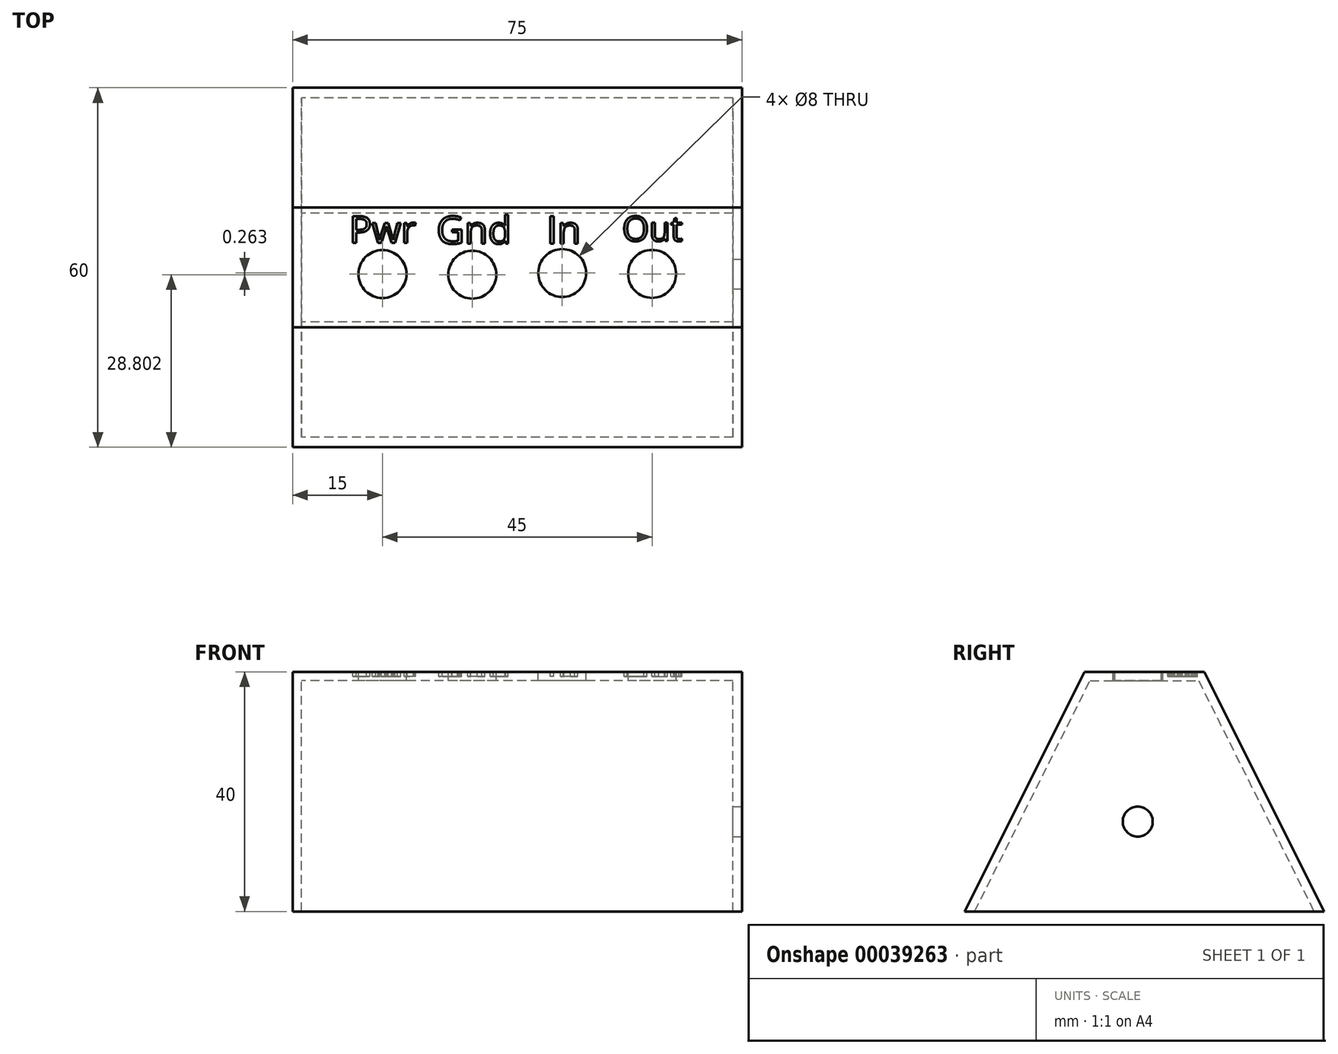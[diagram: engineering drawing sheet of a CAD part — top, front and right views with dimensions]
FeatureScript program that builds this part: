
annotation { "Feature Type Name" : "Feature", "Feature Type Description" : "" }
export const myFeature = defineFeature(function(context is Context, id is Id, definition is map)
    precondition{}
    {
        {
            var Q0;
            Q0=qCreatedBy(makeId("Right.planeOp"),FACE);
            var sketch = newSketch(context, id + "F0", { "sketchPlane" : qUnion([Q0])});
            skLineSegment(sketch, "E0", {"start": v(-28.9, 0) * mm, "end": v(-8.9, 40) * mm});
            skLineSegment(sketch, "E1", {"start": v(-8.9, 40) * mm, "end": v(11.1, 40) * mm});
            skLineSegment(sketch, "E2", {"start": v(11.1, 40) * mm, "end": v(31.1, 0) * mm});
            skLineSegment(sketch, "E3", {"start": v(31.1, 0) * mm, "end": v(-28.9, 0) * mm});
            skSolve(sketch);
        }
        {
            var Q0;
            Q0=makeQuery(id+"F0.imprint","IMPRINT",FACE,{"disambiguationData":[TD([[makeQuery(id+"F0.imprint","IMPRINT",EDGE,{"derivedFrom":sQuery(id+"F0.wireOp",EDGE,"E0")}),-1.0]])]});
            extrude(context, id + "F1", {"entities" : qUnion([Q0]), "depth" : 75 * mm});
        }
        {
            var Q0;
            Q0=makeQuery(id+"F1.opExtrude","SWEPT_FACE",FACE,{"disambiguationData":[OSD([sQuery(id+"F0.wireOp",EDGE,"E3")])]});
            shell(context, id + "F2", {"entities" : qUnion([Q0]), "thickness" : 1.5 * mm});
        }
        {
            var Q0;
            Q0=makeQuery(id+"F1.opExtrude","SWEPT_FACE",FACE,{"disambiguationData":[OSD([sQuery(id+"F0.wireOp",EDGE,"E1")])]});
            var sketch = newSketch(context, id + "F3", { "sketchPlane" : qUnion([Q0])});
            skPoint(sketch, "E4", {"position": v(15, 0) * mm});
            skPoint(sketch, "E5", {"position": v(30, -0.1) * mm});
            skPoint(sketch, "E6", {"position": v(45, 0.17) * mm});
            skPoint(sketch, "E7", {"position": v(60, 0.03) * mm});
            skSolve(sketch);
        }
        {
            var Q0;
            Q0=makeQuery(id+"F1.opExtrude","CAP_FACE",FACE,{"disambiguationData":[OSD([sQuery(id+"F0.wireOp",EDGE,"E0"),sQuery(id+"F0.wireOp",EDGE,"E1"),sQuery(id+"F0.wireOp",EDGE,"E2"),sQuery(id+"F0.wireOp",EDGE,"E3")])],"isStart":false});
            var sketch = newSketch(context, id + "F4", { "sketchPlane" : qUnion([Q0])});
            skPoint(sketch, "E8", {"position": v(0, 15) * mm});
            skSolve(sketch);
        }
        {
            var Q0;
            Q0=sQuery(id+"F4.wireOp",VERTEX,"E8");
            var Q1;
            Q1=makeQuery(id+"F1.opExtrude","SWEPT_BODY",BODY,{"disambiguationData":[OSD([sQuery(id+"F0.wireOp",EDGE,"E0"),sQuery(id+"F0.wireOp",EDGE,"E1"),sQuery(id+"F0.wireOp",EDGE,"E2"),sQuery(id+"F0.wireOp",EDGE,"E3")])]});
            hole(context, id + "F5", {"style" : HoleStyle.SIMPLE, "holeDiameter" : 5 * mm, "endStyle" : HoleEndStyle.BLIND, "holeDepth" : 20 * mm, "locations" : qUnion([Q0]), "scope" : qUnion([Q1])});
        }
        {
            var Q0;
            Q0=makeQuery(id+"F1.opExtrude","SWEPT_FACE",FACE,{"disambiguationData":[OSD([sQuery(id+"F0.wireOp",EDGE,"E1")])]});
            var sketch = newSketch(context, id + "F6", { "sketchPlane" : qUnion([Q0])});
            skText(sketch, "E9", { "text": "Out", "fontName": "OpenSans-Regular.ttf"});
            skText(sketch, "E10", { "text": "In", "fontName": "OpenSans-Regular.ttf"});
            skText(sketch, "E11", { "text": "Gnd", "fontName": "OpenSans-Regular.ttf"});
            skText(sketch, "E12", { "text": "Pwr", "fontName": "OpenSans-Regular.ttf"});
            const initialGuessF6  = {"E9": [0.055, 0.0055, 1, 0, 0.00417], "E10": [0.0424, 0.00506, 1, 0, 0.00462], "E11": [0.024, 0.00506, 1, 0, 0.00462], "E12": [0.00947, 0.00519, 1, 0, 0.0045]};
            skSetInitialGuess(sketch, initialGuessF6);
            skSolve(sketch);
        }
        {
            var Q0;
            Q0 = qSketchRegion(id + "F6", true);
            extrude(context, id + "F7", {"entities" : qUnion([Q0]), "operationType" : NewBodyOperationType.REMOVE, "oppositeDirection" : true, "depth" : 0.75 * mm});
        }
        {
            var Q0;
            Q0=sQuery(id+"F3.wireOp",VERTEX,"E4");
            var Q1;
            Q1=sQuery(id+"F3.wireOp",VERTEX,"E5");
            var Q2;
            Q2=sQuery(id+"F3.wireOp",VERTEX,"E6");
            var Q3;
            Q3=sQuery(id+"F3.wireOp",VERTEX,"E7");
            var Q4;
            Q4=makeQuery(id+"F1.opExtrude","SWEPT_BODY",BODY,{"disambiguationData":[OSD([sQuery(id+"F0.wireOp",EDGE,"E0"),sQuery(id+"F0.wireOp",EDGE,"E1"),sQuery(id+"F0.wireOp",EDGE,"E2"),sQuery(id+"F0.wireOp",EDGE,"E3")])]});
            hole(context, id + "F8", {"style" : HoleStyle.SIMPLE, "holeDiameter" : 8 * mm, "endStyle" : HoleEndStyle.THROUGH, "locations" : qUnion([Q0, Q1, Q2, Q3]), "scope" : qUnion([Q4])});
        }
    });
